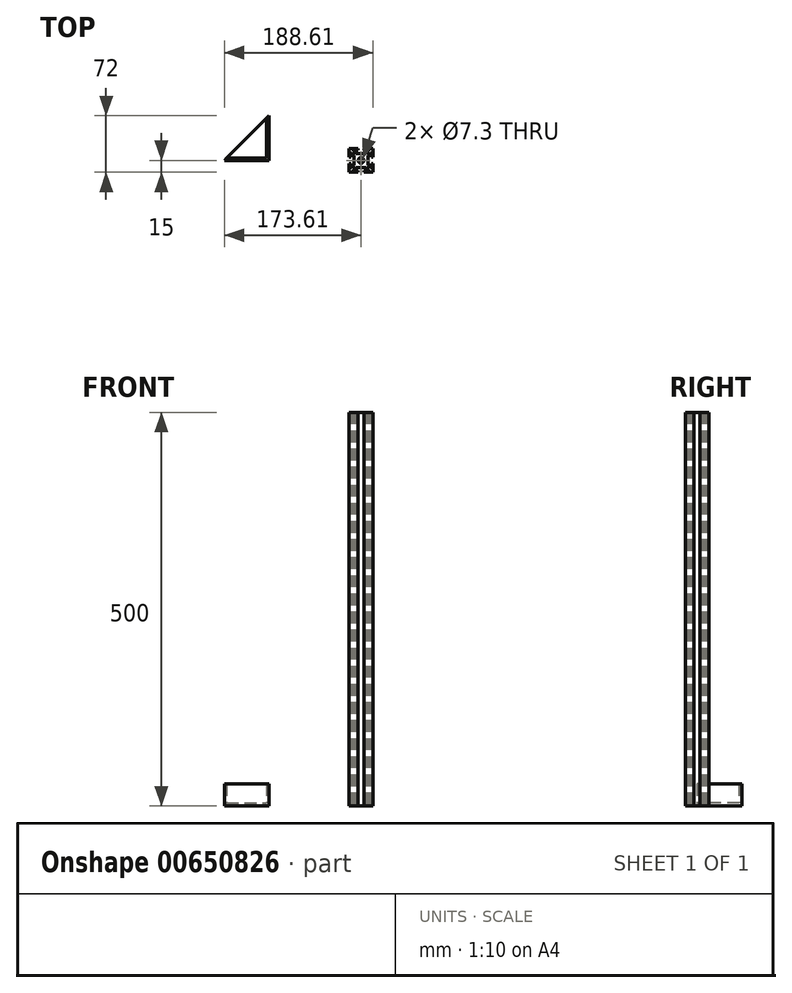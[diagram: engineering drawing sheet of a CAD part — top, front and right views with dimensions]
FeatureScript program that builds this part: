
annotation { "Feature Type Name" : "Feature", "Feature Type Description" : "" }
export const myFeature = defineFeature(function(context is Context, id is Id, definition is map)
    precondition{}
    {
        {
            var Q0;
            Q0=qCreatedBy(makeId("Top.planeOp"),FACE);
            var sketch = newSketch(context, id + "F0", { "sketchPlane" : qUnion([Q0])});
            skPoint(sketch, "E0.middle", {"position": v(0, 0) * mm});
            skCircle(sketch, "E1", {"center": v(0, 0) * mm, "radius": 3.65 * mm});
            skLineSegment(sketch, "E2", {"start": v(-4, 15) * mm, "end": v(-4, 13) * mm});
            skLineSegment(sketch, "E3", {"start": v(-4, 13) * mm, "end": v(-9.26, 13) * mm});
            skLineSegment(sketch, "E4", {"start": v(-6.18, 9) * mm, "end": v(0, 9) * mm});
            skLineSegment(sketch, "E5", {"start": v(-4, 15) * mm, "end": v(-15, 15) * mm});
            skLineSegment(sketch, "E6", {"start": v(-9.26, 13) * mm, "end": v(-9.26, 11.86) * mm});
            skLineSegment(sketch, "E7", {"start": v(-9.26, 11.86) * mm, "end": v(-6.18, 9) * mm});
            skLineSegment(sketch, "E8.MirrorCS", {"start": v(4, 15) * mm, "end": v(15, 15) * mm});
            skLineSegment(sketch, "E9.MirrorCS", {"start": v(4, 13) * mm, "end": v(9.26, 13) * mm});
            skLineSegment(sketch, "E10.MirrorCS", {"start": v(9.26, 13) * mm, "end": v(9.26, 11.86) * mm});
            skLineSegment(sketch, "E11.MirrorCS", {"start": v(9.26, 11.86) * mm, "end": v(6.18, 9) * mm});
            skLineSegment(sketch, "E12.MirrorCS", {"start": v(6.18, 9) * mm, "end": v(0, 9) * mm});
            skLineSegment(sketch, "E13.MirrorCS", {"start": v(4, 15) * mm, "end": v(4, 13) * mm});
            skLineSegment(sketch, "E14.1.0", {"start": v(-15, 4) * mm, "end": v(-15, 15) * mm});
            skLineSegment(sketch, "E14.1.1", {"start": v(-13, 9.26) * mm, "end": v(-11.86, 9.26) * mm});
            skLineSegment(sketch, "E14.1.2", {"start": v(-13, 4) * mm, "end": v(-13, 9.26) * mm});
            skLineSegment(sketch, "E14.1.3", {"start": v(-11.86, -9.26) * mm, "end": v(-9, -6.18) * mm});
            skLineSegment(sketch, "E14.1.4", {"start": v(-15, 4) * mm, "end": v(-13, 4) * mm});
            skLineSegment(sketch, "E14.1.5", {"start": v(-9, -6.18) * mm, "end": v(-9, 0) * mm});
            skLineSegment(sketch, "E14.1.6", {"start": v(-13, -9.26) * mm, "end": v(-11.86, -9.26) * mm});
            skLineSegment(sketch, "E14.1.7", {"start": v(-13, -4) * mm, "end": v(-13, -9.26) * mm});
            skLineSegment(sketch, "E14.1.8", {"start": v(-15, -4) * mm, "end": v(-15, -15) * mm});
            skLineSegment(sketch, "E14.1.9", {"start": v(-11.86, 9.26) * mm, "end": v(-9, 6.18) * mm});
            skLineSegment(sketch, "E14.1.10", {"start": v(-15, -4) * mm, "end": v(-13, -4) * mm});
            skLineSegment(sketch, "E14.1.11", {"start": v(-9, 6.18) * mm, "end": v(-9, 0) * mm});
            skLineSegment(sketch, "E14.2.0", {"start": v(-4, -15) * mm, "end": v(-15, -15) * mm});
            skLineSegment(sketch, "E14.2.1", {"start": v(-9.26, -13) * mm, "end": v(-9.26, -11.86) * mm});
            skLineSegment(sketch, "E14.2.2", {"start": v(-4, -13) * mm, "end": v(-9.26, -13) * mm});
            skLineSegment(sketch, "E14.2.3", {"start": v(9.26, -11.86) * mm, "end": v(6.18, -9) * mm});
            skLineSegment(sketch, "E14.2.4", {"start": v(-4, -15) * mm, "end": v(-4, -13) * mm});
            skLineSegment(sketch, "E14.2.5", {"start": v(6.18, -9) * mm, "end": v(0, -9) * mm});
            skLineSegment(sketch, "E14.2.6", {"start": v(9.26, -13) * mm, "end": v(9.26, -11.86) * mm});
            skLineSegment(sketch, "E14.2.7", {"start": v(4, -13) * mm, "end": v(9.26, -13) * mm});
            skLineSegment(sketch, "E14.2.8", {"start": v(4, -15) * mm, "end": v(15, -15) * mm});
            skLineSegment(sketch, "E14.2.9", {"start": v(-9.26, -11.86) * mm, "end": v(-6.18, -9) * mm});
            skLineSegment(sketch, "E14.2.10", {"start": v(4, -15) * mm, "end": v(4, -13) * mm});
            skLineSegment(sketch, "E14.2.11", {"start": v(-6.18, -9) * mm, "end": v(0, -9) * mm});
            skLineSegment(sketch, "E14.3.0", {"start": v(15, -4) * mm, "end": v(15, -15) * mm});
            skLineSegment(sketch, "E14.3.1", {"start": v(13, -9.26) * mm, "end": v(11.86, -9.26) * mm});
            skLineSegment(sketch, "E14.3.2", {"start": v(13, -4) * mm, "end": v(13, -9.26) * mm});
            skLineSegment(sketch, "E14.3.3", {"start": v(11.86, 9.26) * mm, "end": v(9, 6.18) * mm});
            skLineSegment(sketch, "E14.3.4", {"start": v(15, -4) * mm, "end": v(13, -4) * mm});
            skLineSegment(sketch, "E14.3.5", {"start": v(9, 6.18) * mm, "end": v(9, 0) * mm});
            skLineSegment(sketch, "E14.3.6", {"start": v(13, 9.26) * mm, "end": v(11.86, 9.26) * mm});
            skLineSegment(sketch, "E14.3.7", {"start": v(13, 4) * mm, "end": v(13, 9.26) * mm});
            skLineSegment(sketch, "E14.3.8", {"start": v(15, 4) * mm, "end": v(15, 15) * mm});
            skLineSegment(sketch, "E14.3.9", {"start": v(11.86, -9.26) * mm, "end": v(9, -6.18) * mm});
            skLineSegment(sketch, "E14.3.10", {"start": v(15, 4) * mm, "end": v(13, 4) * mm});
            skLineSegment(sketch, "E14.3.11", {"start": v(9, -6.18) * mm, "end": v(9, 0) * mm});
            skSolve(sketch);
        }
        {
            var Q0;
            Q0=makeQuery(id+"F0.imprint","IMPRINT",FACE,{"disambiguationData":[TD([[makeQuery(id+"F0.imprint","IMPRINT",EDGE,{"derivedFrom":sQuery(id+"F0.wireOp",EDGE,"E1")}),-1.0]])]});
            extrude(context, id + "F1", {"entities" : qUnion([Q0]), "depth" : 500 * mm, "offsetDistance" : 25 * mm});
        }
        {
            var Q0;
            Q0=qCreatedBy(makeId("Top.planeOp"),FACE);
            var sketch = newSketch(context, id + "F2", { "sketchPlane" : qUnion([Q0])});
            skLineSegment(sketch, "E15", {"start": v(-173.61, 0) * mm, "end": v(-116.61, 0) * mm});
            skLineSegment(sketch, "E16", {"start": v(-116.61, 0) * mm, "end": v(-116.61, 57) * mm});
            skLineSegment(sketch, "E17", {"start": v(-116.61, 57) * mm, "end": v(-173.61, 0) * mm});
            skLineSegment(sketch, "E18", {"start": v(-170.84, 2.78) * mm, "end": v(-120.07, 2.78) * mm});
            skLineSegment(sketch, "E19", {"start": v(-120.07, 2.78) * mm, "end": v(-120.07, 53.55) * mm});
            skSolve(sketch);
        }
        {
            var Q0;
            Q0=makeQuery(id+"F2.imprint","IMPRINT",FACE,{"disambiguationData":[TD([[makeQuery(id+"F2.imprint","IMPRINT",EDGE,{"derivedFrom":sQuery(id+"F2.wireOp",EDGE,"E15")}),1.0]])]});
            extrude(context, id + "F3", {"entities" : qUnion([Q0]), "depth" : 28 * mm, "offsetDistance" : 25 * mm});
        }
        {
            var Q0;
            {var subQ0=sQuery(id+"F2.wireOp",EDGE,"E18");Q0=makeQuery(id+"F2.imprint","IMPRINT",FACE,{"disambiguationData":[TD([[makeQuery(id+"F2.imprint","IMPRINT",EDGE,{"derivedFrom":subQ0}),1.0]])]});}
            extrude(context, id + "F4", {"entities" : qUnion([Q0]), "operationType" : NewBodyOperationType.ADD, "depth" : 4 * mm, "offsetDistance" : 25 * mm});
        }
        {
            var Q0;
            Q0=makeQuery(id+"F0.imprint","IMPRINT",FACE,{"disambiguationData":[TD([[makeQuery(id+"F0.imprint","IMPRINT",EDGE,{"derivedFrom":sQuery(id+"F0.wireOp",EDGE,"E1")}),-1.0]])]});
            extrude(context, id + "F5", {"entities" : qUnion([Q0]), "depth" : 500 * mm, "offsetDistance" : 25 * mm});
        }
    });
